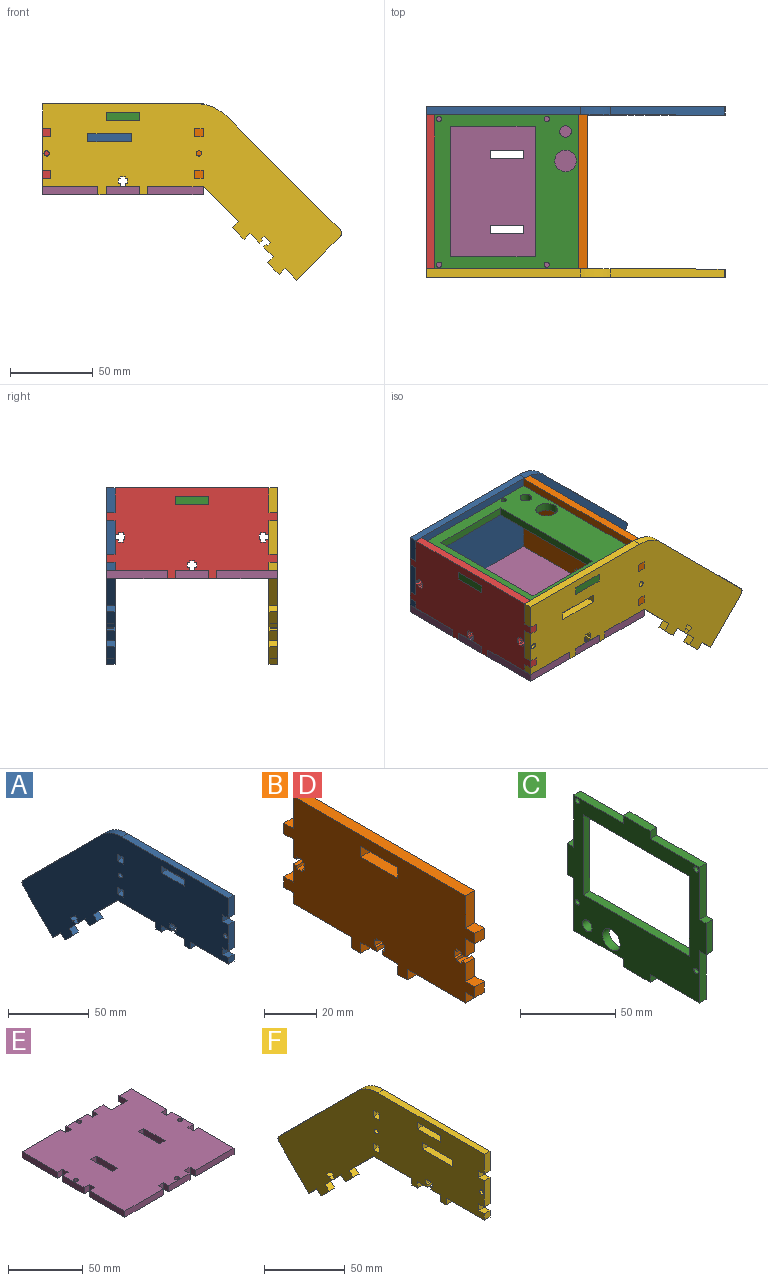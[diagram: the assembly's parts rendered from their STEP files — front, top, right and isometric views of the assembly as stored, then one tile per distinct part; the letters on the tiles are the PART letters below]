
ASSEMBLY  parts=6 mates=5
PART A: 68 faces, bbox 5x180.6x106.6 mm
  f0: plane 5x5mm, normal (0,-1,0), area 25mm2, adj f1,f65,f66,f67
  f1: plane 20x5mm, normal (0,0,1), area 100mm2, adj f0,f2,f66,f67
  f2: plane 5x5mm, normal (0,1,0), area 25mm2, adj f1,f65,f66,f67
  f3: plane 5x5mm, normal (0,0,-1), area 25mm2, adj f4,f60,f66,f67
  f4: plane 5x5mm, normal (0,-1,0), area 25mm2, adj f3,f5,f66,f67
  f5: plane 5x5mm, normal (0,0,1), area 25mm2, adj f4,f60,f66,f67
  f6: plane 5x5mm, normal (0,0,-1), area 25mm2, adj f7,f61,f66,f67
  f7: plane 5x5mm, normal (0,-1,0), area 25mm2, adj f6,f8,f66,f67
  f8: plane 5x5mm, normal (0,0,1), area 25mm2, adj f7,f61,f66,f67
  f9: plane 5x3.54mm, normal (0,0.71,-0.71), area 25mm2, adj f10,f64,f66,f67
  f10: plane 5.94x5.94mm, normal (0,-0.71,-0.71), area 42mm2, adj f9,f11,f66,f67
  f11: plane 5x1.77mm, normal (0,0.71,-0.71), area 12.5mm2, adj f10,f12,f66,f67
  f12: plane 5x0.81mm, normal (0,0.71,0.71), area 5.8mm2, adj f11,f13,f66,f67
  f13: plane 5x1.77mm, normal (0,0.71,-0.71), area 12.5mm2, adj f12,f14,f66,f67
  f14: plane 5x3.89mm, normal (0,-0.71,-0.71), area 27.5mm2, adj f13,f15,f66,f67
  f15: plane 5x1.77mm, normal (0,-0.71,0.71), area 12.5mm2, adj f14,f16,f66,f67
  f16: plane 5x0.81mm, normal (0,0.71,0.71), area 5.8mm2, adj f15,f17,f66,f67
  f17: plane 5x1.77mm, normal (0,-0.71,0.71), area 12.5mm2, adj f16,f18,f66,f67
  f18: plane 5.94x5.94mm, normal (0,-0.71,-0.71), area 42mm2, adj f17,f19,f66,f67
  f19: plane 5x3.54mm, normal (0,-0.71,0.71), area 25mm2, adj f18,f20,f66,f67
  f20: plane 7.07x7.07mm, normal (0,-0.71,-0.71), area 50mm2, adj f19,f21,f66,f67
  f21: plane 5x3.54mm, normal (0,0.71,-0.71), area 25mm2, adj f20,f22,f66,f67
  f22: plane 7.07x7.07mm, normal (0,-0.71,-0.71), area 50mm2, adj f21,f23,f66,f67
  f23: plane 26.16x26.16mm, normal (0,0.71,-0.71), area 185mm2, adj f22,f24,f66,f67
  f24: cylinder r=3mm len=5mm, axis (-1,0,0), area 23.6mm2, adj f23,f25,f66,f67
  f25: plane 68.84x68.84mm, normal (0,0.71,0.71), area 486.8mm2, adj f24,f26,f66,f67
  f26: cylinder r=25mm len=17.68mm, axis (-1,0,0), area 98.2mm2, adj f25,f27,f66,f67
  f27: plane 93.21x5mm, normal (0,0,1), area 466.1mm2, adj f26,f28,f66,f67
  f28: plane 15x5mm, normal (0,-1,0), area 75mm2, adj f27,f29,f66,f67
  f29: plane 5x5mm, normal (0,0,-1), area 25mm2, adj f28,f30,f66,f67
  f30: plane 5x5mm, normal (0,-1,0), area 25mm2, adj f29,f31,f66,f67
  f31: plane 5x5mm, normal (0,0,1), area 25mm2, adj f30,f32,f66,f67
  f32: plane 20x5mm, normal (0,-1,0), area 100mm2, adj f31,f33,f66,f67
  f33: plane 5x5mm, normal (0,0,-1), area 25mm2, adj f32,f34,f66,f67
  f34: plane 5x5mm, normal (0,-1,0), area 25mm2, adj f33,f35,f66,f67
  f35: plane 5x5mm, normal (0,0,1), area 25mm2, adj f34,f36,f66,f67
  f36: plane 5x5mm, normal (0,-1,0), area 25mm2, adj f35,f37,f66,f67
  f37: plane 33.5x5mm, normal (0,0,-1), area 167.5mm2, adj f36,f38,f66,f67
  f38: plane 5x5mm, normal (0,-1,0), area 25mm2, adj f37,f39,f66,f67
  f39: plane 5x5mm, normal (0,0,-1), area 25mm2, adj f38,f40,f66,f67
  f40: plane 5x5mm, normal (0,1,0), area 25mm2, adj f39,f41,f66,f67
  f41: plane 8.5x5mm, normal (0,0,-1), area 42.5mm2, adj f40,f42,f66,f67
  f42: plane 5x2mm, normal (0,1,0), area 10mm2, adj f41,f43,f66,f67
  f43: plane 5x1.25mm, normal (0,0,1), area 6.3mm2, adj f42,f44,f66,f67
  f44: plane 5x3mm, normal (0,1,0), area 15mm2, adj f43,f45,f66,f67
  f45: plane 5x1.25mm, normal (0,0,-1), area 6.3mm2, adj f44,f46,f66,f67
  f46: plane 5x1mm, normal (0,1,0), area 5mm2, adj f45,f47,f66,f67
  f47: plane 5x3mm, normal (0,0,-1), area 15mm2, adj f46,f48,f66,f67
  f48: plane 5x1mm, normal (0,-1,0), area 5mm2, adj f47,f49,f66,f67
  f49: plane 5x1.25mm, normal (0,0,-1), area 6.2mm2, adj f48,f50,f66,f67
  f50: plane 5x3mm, normal (0,-1,0), area 15mm2, adj f49,f51,f66,f67
  f51: plane 5x1.25mm, normal (0,0,1), area 6.2mm2, adj f50,f52,f66,f67
  f52: plane 5x2mm, normal (0,-1,0), area 10mm2, adj f51,f53,f66,f67
  f53: plane 8.5x5mm, normal (0,0,-1), area 42.5mm2, adj f52,f54,f66,f67
  f54: plane 5x5mm, normal (0,-1,0), area 25mm2, adj f53,f55,f66,f67
  f55: plane 5x5mm, normal (0,0,-1), area 25mm2, adj f54,f56,f66,f67
  f56: plane 5x5mm, normal (0,1,0), area 25mm2, adj f55,f57,f66,f67
  f57: plane 33.5x5mm, normal (0,0,-1), area 167.5mm2, adj f56,f58,f66,f67
  f58: plane 21.21x21.21mm, normal (0,-0.71,-0.71), area 150mm2, adj f57,f59,f66,f67
  f59: plane 5x3.54mm, normal (0,-0.71,0.71), area 25mm2, adj f58,f64,f66,f67
  f60: plane 5x5mm, normal (0,1,0), area 25mm2, adj f3,f5,f66,f67
  f61: plane 5x5mm, normal (0,1,0), area 25mm2, adj f6,f8,f66,f67
  f62: cylinder r=1.6mm len=5mm, axis (-1,0,0), area 50.3mm2, adj f66,f67
  f63: cylinder r=1.6mm len=5mm, axis (-1,0,0), area 50.3mm2, adj f66,f67
  f64: plane 7.07x7.07mm, normal (0,-0.71,-0.71), area 50mm2, adj f9,f59,f66,f67
  f65: plane 20x5mm, normal (0,0,-1), area 100mm2, adj f0,f2,f66,f67
  f66: plane 180.61x106.57mm, normal (1,0,0), area 8699.7mm2, adj f0,f1,f2,f3,f4,f5,f6,f7
  f67: plane 180.61x106.57mm, normal (-1,0,0), area 8699.7mm2, adj f0,f1,f2,f3,f4,f5,f6,f7
PART B: 70 faces, bbox 5x103x55 mm
  f0: plane 20x5mm, normal (0,0,1), area 100mm2, adj f1,f67,f68,f69
  f1: plane 5x5mm, normal (0,1,0), area 25mm2, adj f0,f2,f68,f69
  f2: plane 20x5mm, normal (0,0,-1), area 100mm2, adj f1,f67,f68,f69
  f3: plane 5x5mm, normal (0,1,0), area 25mm2, adj f4,f66,f68,f69
  f4: plane 5x5mm, normal (0,0,1), area 25mm2, adj f3,f5,f68,f69
  f5: plane 15x5mm, normal (0,1,0), area 75mm2, adj f4,f6,f68,f69
  f6: plane 93x5mm, normal (0,0,1), area 465mm2, adj f5,f7,f68,f69
  f7: plane 15x5mm, normal (0,-1,0), area 75mm2, adj f6,f8,f68,f69
  f8: plane 5x5mm, normal (0,0,1), area 25mm2, adj f7,f9,f68,f69
  f9: plane 5x5mm, normal (0,-1,0), area 25mm2, adj f8,f10,f68,f69
  f10: plane 5x5mm, normal (0,0,-1), area 25mm2, adj f9,f11,f68,f69
  f11: plane 8.5x5mm, normal (0,-1,0), area 42.5mm2, adj f10,f12,f68,f69
  f12: plane 5x2mm, normal (0,0,-1), area 10mm2, adj f11,f13,f68,f69
  f13: plane 5x1.25mm, normal (0,1,0), area 6.3mm2, adj f12,f14,f68,f69
  f14: plane 5x3mm, normal (0,0,-1), area 15mm2, adj f13,f15,f68,f69
  f15: plane 5x1.25mm, normal (0,-1,0), area 6.3mm2, adj f14,f16,f68,f69
  f16: plane 5x1mm, normal (0,0,-1), area 5mm2, adj f15,f17,f68,f69
  f17: plane 5x3mm, normal (0,-1,0), area 15mm2, adj f16,f18,f68,f69
  f18: plane 5x1mm, normal (0,0,1), area 5mm2, adj f17,f19,f68,f69
  f19: plane 5x1.25mm, normal (0,-1,0), area 6.2mm2, adj f18,f20,f68,f69
  f20: plane 5x3mm, normal (0,0,1), area 15mm2, adj f19,f21,f68,f69
  f21: plane 5x1.25mm, normal (0,1,0), area 6.2mm2, adj f20,f22,f68,f69
  f22: plane 5x2mm, normal (0,0,1), area 10mm2, adj f21,f23,f68,f69
  f23: plane 8.5x5mm, normal (0,-1,0), area 42.5mm2, adj f22,f24,f68,f69
  f24: plane 5x5mm, normal (0,0,1), area 25mm2, adj f23,f25,f68,f69
  f25: plane 5x5mm, normal (0,-1,0), area 25mm2, adj f24,f26,f68,f69
  f26: plane 5x5mm, normal (0,0,-1), area 25mm2, adj f25,f27,f68,f69
  f27: plane 5x5mm, normal (0,-1,0), area 25mm2, adj f26,f28,f68,f69
  f28: plane 31.5x5mm, normal (0,0,-1), area 157.5mm2, adj f27,f29,f68,f69
  f29: plane 5x5mm, normal (0,-1,0), area 25mm2, adj f28,f30,f68,f69
  f30: plane 5x5mm, normal (0,0,-1), area 25mm2, adj f29,f31,f68,f69
  f31: plane 5x5mm, normal (0,1,0), area 25mm2, adj f30,f32,f68,f69
  f32: plane 8.5x5mm, normal (0,0,-1), area 42.5mm2, adj f31,f33,f68,f69
  f33: plane 5x2mm, normal (0,1,0), area 10mm2, adj f32,f34,f68,f69
  f34: plane 5x1.25mm, normal (0,0,1), area 6.3mm2, adj f33,f35,f68,f69
  f35: plane 5x3mm, normal (0,1,0), area 15mm2, adj f34,f36,f68,f69
  f36: plane 5x1.25mm, normal (0,0,-1), area 6.3mm2, adj f35,f37,f68,f69
  f37: plane 5x1mm, normal (0,1,0), area 5mm2, adj f36,f38,f68,f69
  f38: plane 5x3mm, normal (0,0,-1), area 15mm2, adj f37,f39,f68,f69
  f39: plane 5x1mm, normal (0,-1,0), area 5mm2, adj f38,f40,f68,f69
  f40: plane 5x1.25mm, normal (0,0,-1), area 6.3mm2, adj f39,f41,f68,f69
  f41: plane 5x3mm, normal (0,-1,0), area 15mm2, adj f40,f42,f68,f69
  f42: plane 5x1.25mm, normal (0,0,1), area 6.3mm2, adj f41,f43,f68,f69
  f43: plane 5x2mm, normal (0,-1,0), area 10mm2, adj f42,f44,f68,f69
  f44: plane 8.5x5mm, normal (0,0,-1), area 42.5mm2, adj f43,f45,f68,f69
  f45: plane 5x5mm, normal (0,-1,0), area 25mm2, adj f44,f46,f68,f69
  f46: plane 5x5mm, normal (0,0,-1), area 25mm2, adj f45,f47,f68,f69
  f47: plane 5x5mm, normal (0,1,0), area 25mm2, adj f46,f48,f68,f69
  f48: plane 31.5x5mm, normal (0,0,-1), area 157.5mm2, adj f47,f49,f68,f69
  f49: plane 5x5mm, normal (0,1,0), area 25mm2, adj f48,f50,f68,f69
  f50: plane 5x5mm, normal (0,0,-1), area 25mm2, adj f49,f51,f68,f69
  f51: plane 5x5mm, normal (0,1,0), area 25mm2, adj f50,f52,f68,f69
  f52: plane 5x5mm, normal (0,0,1), area 25mm2, adj f51,f53,f68,f69
  f53: plane 8.5x5mm, normal (0,1,0), area 42.5mm2, adj f52,f54,f68,f69
  f54: plane 5x2mm, normal (0,0,1), area 10mm2, adj f53,f55,f68,f69
  f55: plane 5x1.25mm, normal (0,-1,0), area 6.2mm2, adj f54,f56,f68,f69
  f56: plane 5x3mm, normal (0,0,1), area 15mm2, adj f55,f57,f68,f69
  f57: plane 5x1.25mm, normal (0,1,0), area 6.2mm2, adj f56,f58,f68,f69
  f58: plane 5x1mm, normal (0,0,1), area 5mm2, adj f57,f59,f68,f69
  f59: plane 5x3mm, normal (0,1,0), area 15mm2, adj f58,f60,f68,f69
  f60: plane 5x1mm, normal (0,0,-1), area 5mm2, adj f59,f61,f68,f69
  f61: plane 5x1.25mm, normal (0,1,0), area 6.3mm2, adj f60,f62,f68,f69
  f62: plane 5x3mm, normal (0,0,-1), area 15mm2, adj f61,f63,f68,f69
  f63: plane 5x1.25mm, normal (0,-1,0), area 6.3mm2, adj f62,f64,f68,f69
  f64: plane 5x2mm, normal (0,0,-1), area 10mm2, adj f63,f65,f68,f69
  f65: plane 8.5x5mm, normal (0,1,0), area 42.5mm2, adj f64,f66,f68,f69
  f66: plane 5x5mm, normal (0,0,-1), area 25mm2, adj f3,f65,f68,f69
  f67: plane 5x5mm, normal (0,-1,0), area 25mm2, adj f0,f2,f68,f69
  f68: plane 103x55mm, normal (1,0,0), area 4623.5mm2, adj f0,f1,f2,f3,f4,f5,f6,f7
  f69: plane 103x55mm, normal (-1,0,0), area 4623.5mm2, adj f0,f1,f2,f3,f4,f5,f6,f7
PART C: 32 faces, bbox 5x103x97 mm
  f0: plane 78.7x5mm, normal (0,0,1), area 393.5mm2, adj f1,f29,f30,f31
  f1: plane 51.25x5mm, normal (0,1,0), area 256.2mm2, adj f0,f2,f30,f31
  f2: plane 78.7x5mm, normal (0,0,-1), area 393.5mm2, adj f1,f29,f30,f31
  f3: plane 5x5mm, normal (0,1,0), area 25mm2, adj f4,f28,f30,f31
  f4: plane 20x5mm, normal (0,0,1), area 100mm2, adj f3,f5,f30,f31
  f5: plane 5x5mm, normal (0,-1,0), area 25mm2, adj f4,f6,f30,f31
  f6: plane 36.5x5mm, normal (0,0,1), area 182.5mm2, adj f5,f7,f30,f31
  f7: plane 33.5x5mm, normal (0,-1,0), area 167.5mm2, adj f6,f8,f30,f31
  f8: plane 5x5mm, normal (0,0,1), area 25mm2, adj f7,f9,f30,f31
  f9: plane 20x5mm, normal (0,-1,0), area 100mm2, adj f8,f10,f30,f31
  f10: plane 5x5mm, normal (0,0,-1), area 25mm2, adj f9,f11,f30,f31
  f11: plane 33.5x5mm, normal (0,-1,0), area 167.5mm2, adj f10,f12,f30,f31
  f12: plane 36.5x5mm, normal (0,0,-1), area 182.5mm2, adj f11,f13,f30,f31
  f13: plane 5x5mm, normal (0,-1,0), area 25mm2, adj f12,f14,f30,f31
  f14: plane 20x5mm, normal (0,0,-1), area 100mm2, adj f13,f15,f30,f31
  f15: plane 5x5mm, normal (0,1,0), area 25mm2, adj f14,f16,f30,f31
  f16: plane 36.5x5mm, normal (0,0,-1), area 182.5mm2, adj f15,f17,f30,f31
  f17: plane 33.5x5mm, normal (0,1,0), area 167.5mm2, adj f16,f18,f30,f31
  f18: plane 5x5mm, normal (0,0,-1), area 25mm2, adj f17,f19,f30,f31
  f19: plane 20x5mm, normal (0,1,0), area 100mm2, adj f18,f20,f30,f31
  f20: plane 5x5mm, normal (0,0,1), area 25mm2, adj f19,f21,f30,f31
  f21: plane 33.5x5mm, normal (0,1,0), area 167.5mm2, adj f20,f28,f30,f31
  f22: cylinder r=3.5mm len=7mm, axis (-1,0,0), area 110mm2, adj f30,f31
  f23: cylinder r=6.5mm len=13mm, axis (-1,0,0), area 204.2mm2, adj f30,f31
  f24: cylinder r=1.6mm len=5mm, axis (-1,0,0), area 50.3mm2, adj f30,f31
  f25: cylinder r=1.6mm len=5mm, axis (-1,0,0), area 50.3mm2, adj f30,f31
  f26: cylinder r=1.6mm len=5mm, axis (-1,0,0), area 50.3mm2, adj f30,f31
  f27: cylinder r=1.6mm len=5mm, axis (-1,0,0), area 50.3mm2, adj f30,f31
  f28: plane 36.5x5mm, normal (0,0,1), area 182.5mm2, adj f3,f21,f30,f31
  f29: plane 51.25x5mm, normal (0,-1,0), area 256.2mm2, adj f0,f2,f30,f31
  f30: plane 103x97mm, normal (1,0,0), area 4254.2mm2, adj f0,f1,f2,f3,f4,f5,f6,f7
  f31: plane 103x97mm, normal (-1,0,0), area 4254.2mm2, adj f0,f1,f2,f3,f4,f5,f6,f7
PART D: same geometry as B
PART E: 54 faces, bbox 103x97x5 mm
  f0: plane 5x5mm, normal (0,-1,0), area 25mm2, adj f1,f46,f52,f53
  f1: plane 20x5mm, normal (-1,0,0), area 100mm2, adj f0,f2,f52,f53
  f2: plane 5x5mm, normal (0,1,0), area 25mm2, adj f1,f46,f52,f53
  f3: plane 5x5mm, normal (-1,0,0), area 25mm2, adj f4,f47,f52,f53
  f4: plane 20x5mm, normal (0,-1,0), area 100mm2, adj f3,f5,f52,f53
  f5: plane 5x5mm, normal (1,0,0), area 25mm2, adj f4,f6,f52,f53
  f6: plane 5x5mm, normal (0,-1,0), area 25mm2, adj f5,f7,f52,f53
  f7: plane 5x5mm, normal (-1,0,0), area 25mm2, adj f6,f8,f52,f53
  f8: plane 36.5x5mm, normal (0,-1,0), area 182.5mm2, adj f7,f9,f52,f53
  f9: plane 33.5x5mm, normal (1,0,0), area 167.5mm2, adj f8,f10,f52,f53
  f10: plane 5x5mm, normal (0,1,0), area 25mm2, adj f9,f11,f52,f53
  f11: plane 5x5mm, normal (1,0,0), area 25mm2, adj f10,f12,f52,f53
  f12: plane 5x5mm, normal (0,-1,0), area 25mm2, adj f11,f13,f52,f53
  f13: plane 20x5mm, normal (1,0,0), area 100mm2, adj f12,f14,f52,f53
  f14: plane 5x5mm, normal (0,1,0), area 25mm2, adj f13,f15,f52,f53
  f15: plane 5x5mm, normal (1,0,0), area 25mm2, adj f14,f16,f52,f53
  f16: plane 5x5mm, normal (0,-1,0), area 25mm2, adj f15,f17,f52,f53
  f17: plane 33.5x5mm, normal (1,0,0), area 167.5mm2, adj f16,f18,f52,f53
  f18: plane 11.5x5mm, normal (0,1,0), area 57.5mm2, adj f17,f19,f52,f53
  f19: plane 8x5mm, normal (-1,0,0), area 40mm2, adj f18,f20,f52,f53
  f20: plane 15x5mm, normal (0,1,0), area 75mm2, adj f19,f21,f52,f53
  f21: plane 8x5mm, normal (1,0,0), area 40mm2, adj f20,f22,f52,f53
  f22: plane 10x5mm, normal (0,1,0), area 50mm2, adj f21,f23,f52,f53
  f23: plane 5x5mm, normal (-1,0,0), area 25mm2, adj f22,f24,f52,f53
  f24: plane 5x5mm, normal (0,1,0), area 25mm2, adj f23,f25,f52,f53
  f25: plane 5x5mm, normal (1,0,0), area 25mm2, adj f24,f26,f52,f53
  f26: plane 20x5mm, normal (0,1,0), area 100mm2, adj f25,f27,f52,f53
  f27: plane 5x5mm, normal (-1,0,0), area 25mm2, adj f26,f28,f52,f53
  f28: plane 5x5mm, normal (0,1,0), area 25mm2, adj f27,f29,f52,f53
  f29: plane 5x5mm, normal (1,0,0), area 25mm2, adj f28,f30,f52,f53
  f30: plane 36.5x5mm, normal (0,1,0), area 182.5mm2, adj f29,f31,f52,f53
  f31: plane 33.5x5mm, normal (-1,0,0), area 167.5mm2, adj f30,f32,f52,f53
  f32: plane 5x5mm, normal (0,-1,0), area 25mm2, adj f31,f33,f52,f53
  f33: plane 5x5mm, normal (-1,0,0), area 25mm2, adj f32,f34,f52,f53
  f34: plane 5x5mm, normal (0,1,0), area 25mm2, adj f33,f35,f52,f53
  f35: plane 20x5mm, normal (-1,0,0), area 100mm2, adj f34,f36,f52,f53
  f36: plane 5x5mm, normal (0,-1,0), area 25mm2, adj f35,f37,f52,f53
  f37: plane 5x5mm, normal (-1,0,0), area 25mm2, adj f36,f38,f52,f53
  f38: plane 5x5mm, normal (0,1,0), area 25mm2, adj f37,f39,f52,f53
  f39: plane 33.5x5mm, normal (-1,0,0), area 167.5mm2, adj f38,f40,f52,f53
  f40: plane 36.5x5mm, normal (0,-1,0), area 182.5mm2, adj f39,f41,f52,f53
  f41: plane 5x5mm, normal (1,0,0), area 25mm2, adj f40,f47,f52,f53
  f42: plane 5x5mm, normal (0,1,0), area 25mm2, adj f43,f48,f52,f53
  f43: plane 20x5mm, normal (1,0,0), area 100mm2, adj f42,f44,f52,f53
  f44: plane 5x5mm, normal (0,-1,0), area 25mm2, adj f43,f48,f52,f53
  f45: cylinder r=1.6mm len=5mm, axis (0,0,-1), area 50.3mm2, adj f52,f53
  f46: plane 20x5mm, normal (1,0,0), area 100mm2, adj f0,f2,f52,f53
  f47: plane 5x5mm, normal (0,-1,0), area 25mm2, adj f3,f41,f52,f53
  f48: plane 20x5mm, normal (-1,0,0), area 100mm2, adj f42,f44,f52,f53
  f49: cylinder r=1.6mm len=5mm, axis (0,0,-1), area 50.3mm2, adj f52,f53
  f50: cylinder r=1.6mm len=5mm, axis (0,0,-1), area 50.3mm2, adj f52,f53
  f51: cylinder r=1.6mm len=5mm, axis (0,0,-1), area 50.3mm2, adj f52,f53
  f52: plane 103x97mm, normal (0,0,1), area 9438.8mm2, adj f0,f1,f2,f3,f4,f5,f6,f7
  f53: plane 103x97mm, normal (0,0,-1), area 9438.8mm2, adj f0,f1,f2,f3,f4,f5,f6,f7
PART F: 72 faces, bbox 5x180.6x106.6 mm
  f0: plane 5x5mm, normal (0,-1,0), area 25mm2, adj f1,f69,f70,f71
  f1: plane 5x5mm, normal (0,0,1), area 25mm2, adj f0,f2,f70,f71
  f2: plane 5x5mm, normal (0,1,0), area 25mm2, adj f1,f69,f70,f71
  f3: plane 5x5mm, normal (0,-1,0), area 25mm2, adj f4,f63,f70,f71
  f4: plane 20x5mm, normal (0,0,1), area 100mm2, adj f3,f5,f70,f71
  f5: plane 5x5mm, normal (0,1,0), area 25mm2, adj f4,f63,f70,f71
  f6: plane 26.4x5mm, normal (0,0,1), area 132mm2, adj f7,f64,f70,f71
  f7: plane 5x5mm, normal (0,1,0), area 25mm2, adj f6,f8,f70,f71
  f8: plane 26.4x5mm, normal (0,0,-1), area 132mm2, adj f7,f64,f70,f71
  f9: plane 5x5mm, normal (0,0,-1), area 25mm2, adj f10,f65,f70,f71
  f10: plane 5x5mm, normal (0,-1,0), area 25mm2, adj f9,f11,f70,f71
  f11: plane 5x5mm, normal (0,0,1), area 25mm2, adj f10,f65,f70,f71
  f12: plane 5x3.54mm, normal (0,0.71,-0.71), area 25mm2, adj f13,f68,f70,f71
  f13: plane 5.94x5.94mm, normal (0,-0.71,-0.71), area 42mm2, adj f12,f14,f70,f71
  f14: plane 5x1.77mm, normal (0,0.71,-0.71), area 12.5mm2, adj f13,f15,f70,f71
  f15: plane 5x0.81mm, normal (0,0.71,0.71), area 5.8mm2, adj f14,f16,f70,f71
  f16: plane 5x1.77mm, normal (0,0.71,-0.71), area 12.5mm2, adj f15,f17,f70,f71
  f17: plane 5x3.89mm, normal (0,-0.71,-0.71), area 27.5mm2, adj f16,f18,f70,f71
  f18: plane 5x1.77mm, normal (0,-0.71,0.71), area 12.5mm2, adj f17,f19,f70,f71
  f19: plane 5x0.81mm, normal (0,0.71,0.71), area 5.8mm2, adj f18,f20,f70,f71
  f20: plane 5x1.77mm, normal (0,-0.71,0.71), area 12.5mm2, adj f19,f21,f70,f71
  f21: plane 5.94x5.94mm, normal (0,-0.71,-0.71), area 42mm2, adj f20,f22,f70,f71
  f22: plane 5x3.54mm, normal (0,-0.71,0.71), area 25mm2, adj f21,f23,f70,f71
  f23: plane 7.07x7.07mm, normal (0,-0.71,-0.71), area 50mm2, adj f22,f24,f70,f71
  f24: plane 5x3.54mm, normal (0,0.71,-0.71), area 25mm2, adj f23,f25,f70,f71
  f25: plane 7.07x7.07mm, normal (0,-0.71,-0.71), area 50mm2, adj f24,f26,f70,f71
  f26: plane 26.16x26.16mm, normal (0,0.71,-0.71), area 185mm2, adj f25,f27,f70,f71
  f27: cylinder r=3mm len=5mm, axis (-1,0,0), area 23.6mm2, adj f26,f28,f70,f71
  f28: plane 68.84x68.84mm, normal (0,0.71,0.71), area 486.8mm2, adj f27,f29,f70,f71
  f29: cylinder r=25mm len=17.68mm, axis (-1,0,0), area 98.2mm2, adj f28,f30,f70,f71
  f30: plane 93.21x5mm, normal (0,0,1), area 466.1mm2, adj f29,f31,f70,f71
  f31: plane 15x5mm, normal (0,-1,0), area 75mm2, adj f30,f32,f70,f71
  f32: plane 5x5mm, normal (0,0,-1), area 25mm2, adj f31,f33,f70,f71
  f33: plane 5x5mm, normal (0,-1,0), area 25mm2, adj f32,f34,f70,f71
  f34: plane 5x5mm, normal (0,0,1), area 25mm2, adj f33,f35,f70,f71
  f35: plane 20x5mm, normal (0,-1,0), area 100mm2, adj f34,f36,f70,f71
  f36: plane 5x5mm, normal (0,0,-1), area 25mm2, adj f35,f37,f70,f71
  f37: plane 5x5mm, normal (0,-1,0), area 25mm2, adj f36,f38,f70,f71
  f38: plane 5x5mm, normal (0,0,1), area 25mm2, adj f37,f39,f70,f71
  f39: plane 5x5mm, normal (0,-1,0), area 25mm2, adj f38,f40,f70,f71
  f40: plane 33.5x5mm, normal (0,0,-1), area 167.5mm2, adj f39,f41,f70,f71
  f41: plane 5x5mm, normal (0,-1,0), area 25mm2, adj f40,f42,f70,f71
  f42: plane 5x5mm, normal (0,0,-1), area 25mm2, adj f41,f43,f70,f71
  f43: plane 5x5mm, normal (0,1,0), area 25mm2, adj f42,f44,f70,f71
  f44: plane 8.5x5mm, normal (0,0,-1), area 42.5mm2, adj f43,f45,f70,f71
  f45: plane 5x2mm, normal (0,1,0), area 10mm2, adj f44,f46,f70,f71
  f46: plane 5x1.25mm, normal (0,0,1), area 6.3mm2, adj f45,f47,f70,f71
  f47: plane 5x3mm, normal (0,1,0), area 15mm2, adj f46,f48,f70,f71
  f48: plane 5x1.25mm, normal (0,0,-1), area 6.3mm2, adj f47,f49,f70,f71
  f49: plane 5x1mm, normal (0,1,0), area 5mm2, adj f48,f50,f70,f71
  f50: plane 5x3mm, normal (0,0,-1), area 15mm2, adj f49,f51,f70,f71
  f51: plane 5x1mm, normal (0,-1,0), area 5mm2, adj f50,f52,f70,f71
  f52: plane 5x1.25mm, normal (0,0,-1), area 6.2mm2, adj f51,f53,f70,f71
  f53: plane 5x3mm, normal (0,-1,0), area 15mm2, adj f52,f54,f70,f71
  f54: plane 5x1.25mm, normal (0,0,1), area 6.2mm2, adj f53,f55,f70,f71
  f55: plane 5x2mm, normal (0,-1,0), area 10mm2, adj f54,f56,f70,f71
  f56: plane 8.5x5mm, normal (0,0,-1), area 42.5mm2, adj f55,f57,f70,f71
  f57: plane 5x5mm, normal (0,-1,0), area 25mm2, adj f56,f58,f70,f71
  f58: plane 5x5mm, normal (0,0,-1), area 25mm2, adj f57,f59,f70,f71
  f59: plane 5x5mm, normal (0,1,0), area 25mm2, adj f58,f60,f70,f71
  f60: plane 33.5x5mm, normal (0,0,-1), area 167.5mm2, adj f59,f61,f70,f71
  f61: plane 21.21x21.21mm, normal (0,-0.71,-0.71), area 150mm2, adj f60,f62,f70,f71
  f62: plane 5x3.54mm, normal (0,-0.71,0.71), area 25mm2, adj f61,f68,f70,f71
  f63: plane 20x5mm, normal (0,0,-1), area 100mm2, adj f3,f5,f70,f71
  f64: plane 5x5mm, normal (0,-1,0), area 25mm2, adj f6,f8,f70,f71
  f65: plane 5x5mm, normal (0,1,0), area 25mm2, adj f9,f11,f70,f71
  f66: cylinder r=1.6mm len=5mm, axis (-1,0,0), area 50.3mm2, adj f70,f71
  f67: cylinder r=1.6mm len=5mm, axis (-1,0,0), area 50.3mm2, adj f70,f71
  f68: plane 7.07x7.07mm, normal (0,-0.71,-0.71), area 50mm2, adj f12,f62,f70,f71
  f69: plane 5x5mm, normal (0,0,-1), area 25mm2, adj f0,f2,f70,f71
  f70: plane 180.61x106.57mm, normal (1,0,0), area 8567.7mm2, adj f0,f1,f2,f3,f4,f5,f6,f7
  f71: plane 180.61x106.57mm, normal (-1,0,0), area 8567.7mm2, adj f0,f1,f2,f3,f4,f5,f6,f7
PLACE A rot(axis=(0,0,-1),90deg) t=(-120.11,-3.31,37.05)mm
PLACE B t=(-28.11,-101.31,37.05)mm
PLACE C rot(axis=(0,-1,0),90deg) t=(-28.11,-101.31,77.05)mm fixed
PLACE D t=(-120.11,-101.31,37.05)mm
PLACE E rot(axis=(0,0,-1),90deg) t=(-120.11,-3.31,32.05)mm
PLACE F rot(axis=(0,0,-1),90deg) t=(-120.11,-101.31,37.05)mm
MATE fastened D.f8 <-> F.f32  axis (0,0,1) through (-117.61,-103.81,72.05)mm
MATE fastened C.f20 <-> A.f2  axis (-1,0,0) through (-81.61,-5.81,79.55)mm
MATE fastened C.f13 <-> B.f1  axis (0,-1,0) through (-25.61,-64.81,79.55)mm
MATE fastened C.f8 <-> F.f5  axis (-1,0,0) through (-81.61,-103.81,79.55)mm
MATE fastened E.f5 <-> D.f31  axis (0,-1,0) through (-117.61,-64.81,34.55)mm
